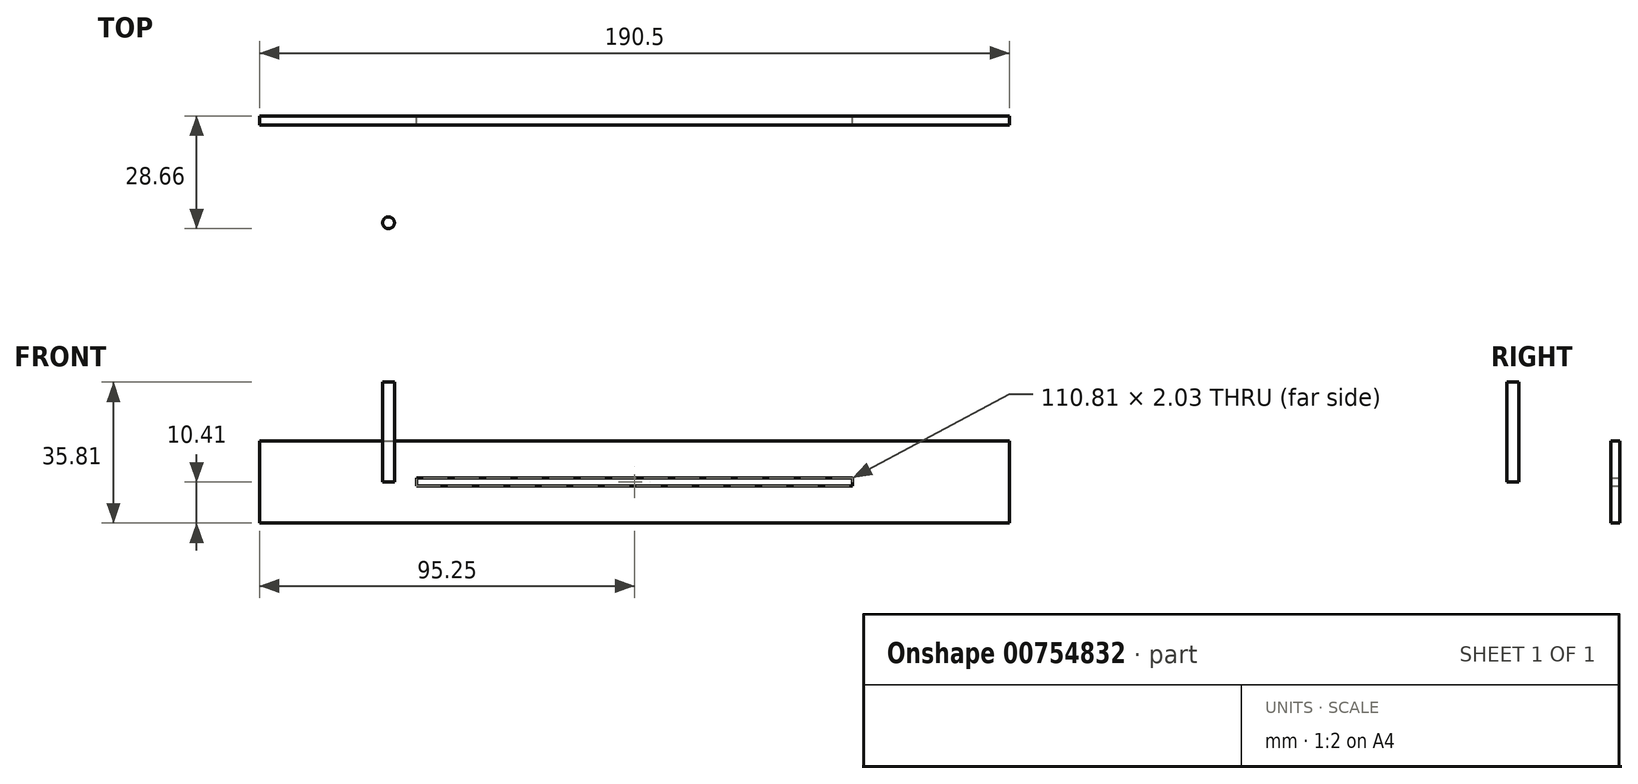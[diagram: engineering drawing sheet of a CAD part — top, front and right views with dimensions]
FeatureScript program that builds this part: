
annotation { "Feature Type Name" : "Feature", "Feature Type Description" : "" }
export const myFeature = defineFeature(function(context is Context, id is Id, definition is map)
    precondition{}
    {
        {
            var Q0;
            Q0=qCreatedBy(makeId("Front.planeOp"),FACE);
            var sketch = newSketch(context, id + "F0", { "sketchPlane" : qUnion([Q0])});
            skLineSegment(sketch, "E0.bottom", {"start": v(-95.25, 10.41) * mm, "end": v(95.25, 10.41) * mm});
            skLineSegment(sketch, "E0.top", {"start": v(-95.25, -10.41) * mm, "end": v(95.25, -10.41) * mm});
            skLineSegment(sketch, "E0.left", {"start": v(-95.25, 10.41) * mm, "end": v(-95.25, -10.41) * mm});
            skLineSegment(sketch, "E0.right", {"start": v(95.25, 10.41) * mm, "end": v(95.25, -10.41) * mm});
            skLineSegment(sketch, "E1.bottom", {"start": v(-55.4, 1.02) * mm, "end": v(55.4, 1.02) * mm});
            skLineSegment(sketch, "E1.top", {"start": v(-55.4, -1.02) * mm, "end": v(55.4, -1.02) * mm});
            skLineSegment(sketch, "E1.left", {"start": v(-55.4, 1.02) * mm, "end": v(-55.4, -1.02) * mm});
            skLineSegment(sketch, "E1.right", {"start": v(55.4, 1.02) * mm, "end": v(55.4, -1.02) * mm});
            skPoint(sketch, "E1.middle", {"position": v(0, 0) * mm});
            skSolve(sketch);
        }
        {
            var Q0;
            Q0=makeQuery(id+"F0.imprint","IMPRINT",FACE,{"disambiguationData":[TD([[makeQuery(id+"F0.imprint","IMPRINT",EDGE,{"derivedFrom":sQuery(id+"F0.wireOp",EDGE,"E0.bottom")}),-1.0]])]});
            extrude(context, id + "F1", {"entities" : qUnion([Q0]), "depth" : 2.3 * mm, "offsetDistance" : 25.4 * mm});
        }
        {
            var Q0;
            Q0=qCreatedBy(makeId("Top.planeOp"),FACE);
            var sketch = newSketch(context, id + "F2", { "sketchPlane" : qUnion([Q0])});
            skCircle(sketch, "E2", {"center": v(-62.5, -27.16) * mm, "radius": 1.5 * mm});
            skSolve(sketch);
        }
        {
            var Q0;
            Q0=makeQuery(id+"F2.imprint","IMPRINT",FACE,{"disambiguationData":[TD([[makeQuery(id+"F2.imprint","IMPRINT",EDGE,{"derivedFrom":sQuery(id+"F2.wireOp",EDGE,"E2")}),1.0]])]});
            extrude(context, id + "F3", {"entities" : qUnion([Q0]), "depth" : 25.4 * mm, "offsetDistance" : 25.4 * mm});
        }
    });
